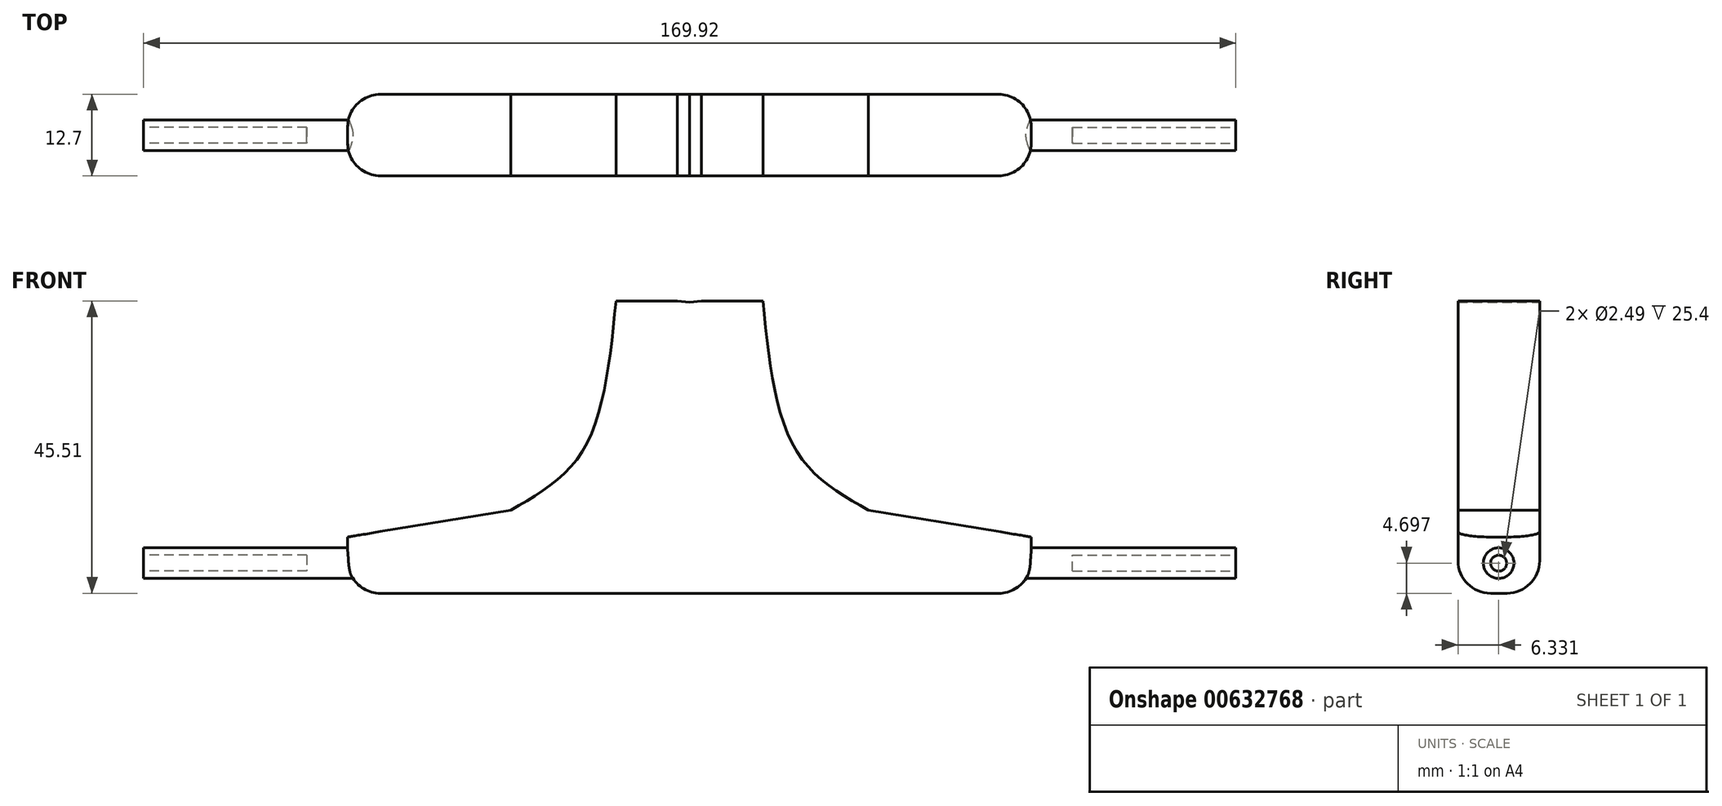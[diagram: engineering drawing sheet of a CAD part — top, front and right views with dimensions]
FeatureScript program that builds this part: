
annotation { "Feature Type Name" : "Feature", "Feature Type Description" : "" }
export const myFeature = defineFeature(function(context is Context, id is Id, definition is map)
    precondition{}
    {
        {
            var Q0;
            Q0=qCreatedBy(makeId("Front.planeOp"),FACE);
            var sketch = newSketch(context, id + "F0", { "sketchPlane" : qUnion([Q0])});
            skLineSegment(sketch, "E0", {"start": v(0, 7.5) * mm, "end": v(-53.17, 7.5) * mm});
            skLineSegment(sketch, "E1", {"start": v(-53.17, 7.5) * mm, "end": v(-53.17, 16.27) * mm});
            skLineSegment(sketch, "E2", {"start": v(-53.17, 16.27) * mm, "end": v(-27.8, 20.47) * mm});
            skLineSegment(sketch, "E3", {"start": v(-11.43, 53) * mm, "end": v(-1.87, 53) * mm});
            skLineSegment(sketch, "E4", {"start": v(-1.87, 53) * mm, "end": v(0, 52.86) * mm});
            skFitSpline(sketch, "E5", {"points": [v(-27.8, 20.47) * mm, v(-16.64, 29.66) * mm, v(-11.43, 53) * mm], "startDerivative": vector(29.07, 16.53) * mm, "endDerivative": vector(4.68, 47.26) * mm});
            skLineSegment(sketch, "E6.MirrorCS", {"start": v(1.87, 53) * mm, "end": v(0, 52.86) * mm});
            skLineSegment(sketch, "E7.MirrorCS", {"start": v(11.43, 53) * mm, "end": v(1.87, 53) * mm});
            skFitSpline(sketch, "E8.MirrorCS", {"points": [v(27.8, 20.47) * mm, v(16.64, 29.66) * mm, v(11.43, 53) * mm], "startDerivative": vector(-29.07, 16.53) * mm, "endDerivative": vector(-4.68, 47.26) * mm});
            skLineSegment(sketch, "E9.MirrorCS", {"start": v(53.17, 16.27) * mm, "end": v(27.8, 20.47) * mm});
            skLineSegment(sketch, "E10.MirrorCS", {"start": v(53.17, 7.5) * mm, "end": v(53.17, 16.27) * mm});
            skLineSegment(sketch, "E11.MirrorCS", {"start": v(0, 7.5) * mm, "end": v(53.17, 7.5) * mm});
            skSolve(sketch);
        }
        {
            var Q0;
            Q0 = qSketchRegion(id + "F0", true);
            extrude(context, id + "F1", {"entities" : qUnion([Q0]), "depth" : 12.7 * mm, "offsetDistance" : 25.4 * mm});
        }
        {
            var Q0;
            Q0=makeQuery(id+"F1.opExtrude","SWEPT_FACE",FACE,{"disambiguationData":[OSD([sQuery(id+"F0.wireOp",EDGE,"E1")])]});
            var sketch = newSketch(context, id + "F2", { "sketchPlane" : qUnion([Q0])});
            skCircle(sketch, "E12", {"center": v(6.37, 12.2) * mm, "radius": 2.38 * mm});
            skSolve(sketch);
        }
        {
            var Q0;
            Q0=makeQuery(id+"F2.imprint","IMPRINT",FACE,{"disambiguationData":[TD([[makeQuery(id+"F2.imprint","IMPRINT",EDGE,{"derivedFrom":sQuery(id+"F2.wireOp",EDGE,"E12")}),1.0]])]});
            extrude(context, id + "F3", {"entities" : qUnion([Q0]), "operationType" : NewBodyOperationType.ADD, "depth" : 31.75 * mm, "offsetDistance" : 25.4 * mm, "hasSecondDirection" : true, "secondDirectionOppositeDirection" : true, "secondDirectionDepth" : 138.18 * mm});
        }
        {
            var Q0;
            Q0=makeQuery(id+"F1.opExtrude","CAP_EDGE",EDGE,{"disambiguationData":[OSD([sQuery(id+"F0.wireOp",EDGE,"E0"),sQuery(id+"F0.wireOp",EDGE,"E11.MirrorCS")])],"isStart":true});
            fillet(context, id + "F4", {"entities" : qUnion([Q0]), "radius" : 5.08 * mm, "tangentPropagation" : true, "allowEdgeOverflow" : false});
        }
        {
            var Q0;
            Q0=makeQuery(id+"F4.opFillet","BLEND_EDGE",EDGE,{"blendedFrom":[makeQuery(id+"F1.opExtrude","CAP_EDGE",EDGE,{"disambiguationData":[OSD([sQuery(id+"F0.wireOp",EDGE,"E0"),sQuery(id+"F0.wireOp",EDGE,"E11.MirrorCS")])],"isStart":true}),makeQuery(id+"F1.opExtrude","SWEPT_FACE",FACE,{"disambiguationData":[OSD([sQuery(id+"F0.wireOp",EDGE,"E1")])]})],"blendedInto":[makeQuery(id+"F1.opExtrude","SWEPT_FACE",FACE,{"disambiguationData":[OSD([sQuery(id+"F0.wireOp",EDGE,"E1")])]})]});
            fillet(context, id + "F5", {"entities" : qUnion([Q0]), "radius" : 5.08 * mm, "tangentPropagation" : true, "allowEdgeOverflow" : false});
        }
        {
            var Q0;
            {var subQ0=sQuery(id+"F0.wireOp",EDGE,"E1");var subQ1=sQuery(id+"F0.wireOp",EDGE,"E0");Q0=makeQuery(id+"F5.opFillet","BLEND_EDGE",EDGE,{"blendedFrom":[makeQuery(id+"F1.opExtrude","SWEPT_EDGE",EDGE,{"disambiguationData":[OSD([subQ1,subQ0])]}),makeQuery(id+"F1.opExtrude","CAP_FACE",FACE,{"disambiguationData":[OSD([subQ1,subQ0,sQuery(id+"F0.wireOp",EDGE,"E2"),sQuery(id+"F0.wireOp",EDGE,"E3"),sQuery(id+"F0.wireOp",EDGE,"E4"),sQuery(id+"F0.wireOp",EDGE,"E5"),sQuery(id+"F0.wireOp",EDGE,"E6.MirrorCS"),sQuery(id+"F0.wireOp",EDGE,"E7.MirrorCS"),sQuery(id+"F0.wireOp",EDGE,"E8.MirrorCS"),sQuery(id+"F0.wireOp",EDGE,"E9.MirrorCS"),sQuery(id+"F0.wireOp",EDGE,"E10.MirrorCS"),sQuery(id+"F0.wireOp",EDGE,"E11.MirrorCS")])],"isStart":false})],"blendedInto":[makeQuery(id+"F1.opExtrude","CAP_FACE",FACE,{"disambiguationData":[OSD([subQ1,subQ0,sQuery(id+"F0.wireOp",EDGE,"E2"),sQuery(id+"F0.wireOp",EDGE,"E3"),sQuery(id+"F0.wireOp",EDGE,"E4"),sQuery(id+"F0.wireOp",EDGE,"E5"),sQuery(id+"F0.wireOp",EDGE,"E6.MirrorCS"),sQuery(id+"F0.wireOp",EDGE,"E7.MirrorCS"),sQuery(id+"F0.wireOp",EDGE,"E8.MirrorCS"),sQuery(id+"F0.wireOp",EDGE,"E9.MirrorCS"),sQuery(id+"F0.wireOp",EDGE,"E10.MirrorCS"),sQuery(id+"F0.wireOp",EDGE,"E11.MirrorCS")])],"isStart":false})]});}
            fillet(context, id + "F6", {"entities" : qUnion([Q0]), "radius" : 5.08 * mm, "tangentPropagation" : true, "allowEdgeOverflow" : false});
        }
        {
            var Q0;
            Q0=makeQuery(id+"F3.opExtrude","CAP_FACE",FACE,{"disambiguationData":[OSD([sQuery(id+"F2.wireOp",EDGE,"E12")])],"isStart":false});
            var sketch = newSketch(context, id + "F7", { "sketchPlane" : qUnion([Q0])});
            skCircle(sketch, "E13", {"center": v(6.37, 12.2) * mm, "radius": 1.25 * mm});
            skSolve(sketch);
        }
        {
            var Q0;
            Q0=makeQuery(id+"F7.imprint","IMPRINT",FACE,{"disambiguationData":[TD([[makeQuery(id+"F7.imprint","IMPRINT",EDGE,{"derivedFrom":sQuery(id+"F7.wireOp",EDGE,"E13")}),1.0]])]});
            extrude(context, id + "F8", {"entities" : qUnion([Q0]), "operationType" : NewBodyOperationType.REMOVE, "oppositeDirection" : true, "depth" : 25.4 * mm, "offsetDistance" : 25.4 * mm});
        }
        {
            var Q0;
            Q0=makeQuery(id+"F1.opExtrude","CAP_EDGE",EDGE,{"disambiguationData":[OSD([sQuery(id+"F0.wireOp",EDGE,"E10.MirrorCS")])],"isStart":false});
            fillet(context, id + "F9", {"entities" : qUnion([Q0]), "radius" : 5.08 * mm, "tangentPropagation" : true, "allowEdgeOverflow" : false});
        }
        {
            var Q0;
            Q0=makeQuery(id+"F3.opExtrude","CAP_FACE",FACE,{"disambiguationData":[OSD([sQuery(id+"F2.wireOp",EDGE,"E12")])],"isStart":true});
            var sketch = newSketch(context, id + "F10", { "sketchPlane" : qUnion([Q0])});
            skCircle(sketch, "E14", {"center": v(-6.37, 12.2) * mm, "radius": 1.25 * mm});
            skSolve(sketch);
        }
        {
            var Q0;
            Q0=makeQuery(id+"F10.imprint","IMPRINT",FACE,{"disambiguationData":[TD([[makeQuery(id+"F10.imprint","IMPRINT",EDGE,{"derivedFrom":sQuery(id+"F10.wireOp",EDGE,"E14")}),1.0]])]});
            extrude(context, id + "F11", {"entities" : qUnion([Q0]), "operationType" : NewBodyOperationType.REMOVE, "oppositeDirection" : true, "depth" : 25.4 * mm, "offsetDistance" : 25.4 * mm});
        }
    });
